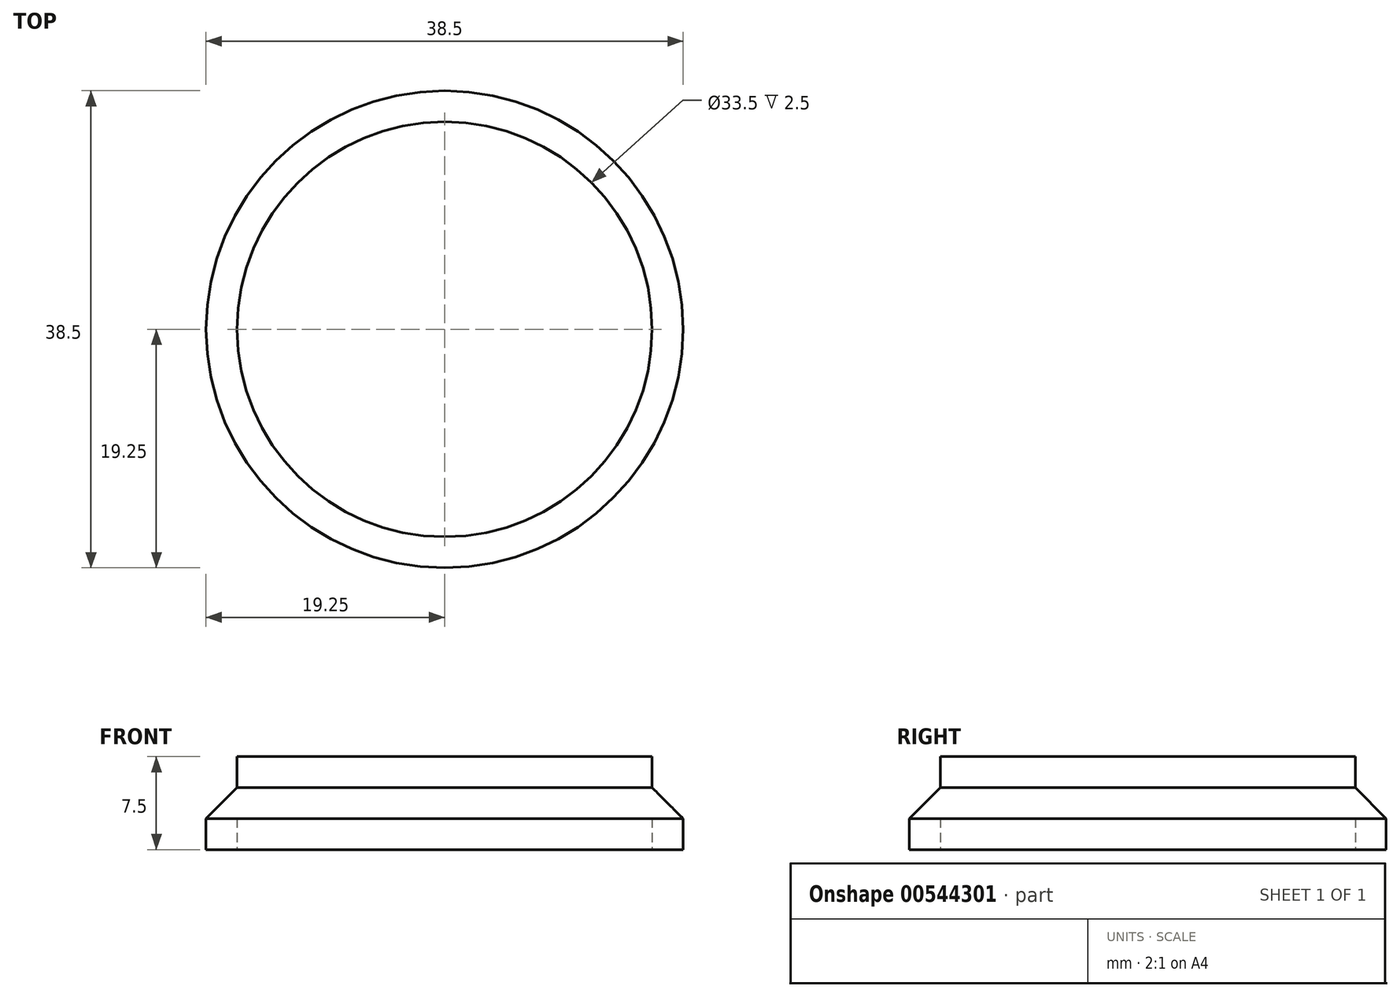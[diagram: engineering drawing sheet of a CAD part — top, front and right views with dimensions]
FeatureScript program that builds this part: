
annotation { "Feature Type Name" : "Feature", "Feature Type Description" : "" }
export const myFeature = defineFeature(function(context is Context, id is Id, definition is map)
    precondition{}
    {
        {
            var Q0;
            Q0=qCreatedBy(makeId("Top.planeOp"),FACE);
            var sketch = newSketch(context, id + "F0", { "sketchPlane" : qUnion([Q0])});
            skCircle(sketch, "E0", {"center": v(0, 0) * mm, "radius": 19.25 * mm});
            skSolve(sketch);
        }
        {
            var Q0;
            Q0 = qSketchRegion(id + "F0", true);
            extrude(context, id + "F1", {"entities" : qUnion([Q0]), "depth" : 5 * mm, "offsetDistance" : 25 * mm});
        }
        {
            var Q0;
            Q0=makeQuery(id+"F1.opExtrude","CAP_FACE",FACE,{"disambiguationData":[OSD([sQuery(id+"F0.wireOp",EDGE,"E0")])],"isStart":false});
            var sketch = newSketch(context, id + "F2", { "sketchPlane" : qUnion([Q0])});
            skCircle(sketch, "E1", {"center": v(0, 0) * mm, "radius": 16.75 * mm});
            skSolve(sketch);
        }
        {
            var Q0;
            Q0=makeQuery(id+"F2.imprint","IMPRINT",FACE,{"disambiguationData":[TD([[makeQuery(id+"F2.imprint","IMPRINT",EDGE,{"derivedFrom":sQuery(id+"F2.wireOp",EDGE,"E1")}),1.0]])]});
            extrude(context, id + "F3", {"entities" : qUnion([Q0]), "operationType" : NewBodyOperationType.ADD, "depth" : 2.5 * mm, "offsetDistance" : 25 * mm});
        }
        {
            var Q0;
            Q0=makeQuery(id+"F1.opExtrude","CAP_FACE",FACE,{"disambiguationData":[OSD([sQuery(id+"F0.wireOp",EDGE,"E0")])],"isStart":true});
            var sketch = newSketch(context, id + "F4", { "sketchPlane" : qUnion([Q0])});
            skCircle(sketch, "E2", {"center": v(0, 0) * mm, "radius": 16.75 * mm});
            skSolve(sketch);
        }
        {
            var Q0;
            Q0=makeQuery(id+"F4.imprint","IMPRINT",FACE,{"disambiguationData":[TD([[makeQuery(id+"F4.imprint","IMPRINT",EDGE,{"derivedFrom":sQuery(id+"F4.wireOp",EDGE,"E2")}),1.0]])]});
            extrude(context, id + "F5", {"entities" : qUnion([Q0]), "operationType" : NewBodyOperationType.REMOVE, "oppositeDirection" : true, "depth" : 2.5 * mm, "offsetDistance" : 25 * mm});
        }
        {
            var Q0;
            Q0=makeQuery(id+"F1.opExtrude","CAP_EDGE",EDGE,{"disambiguationData":[OSD([sQuery(id+"F0.wireOp",EDGE,"E0")])],"isStart":false});
            chamfer(context, id + "F6", {"entities" : qUnion([Q0]), "width" : 2.5 * mm, "tangentPropagation" : true});
        }
    });
